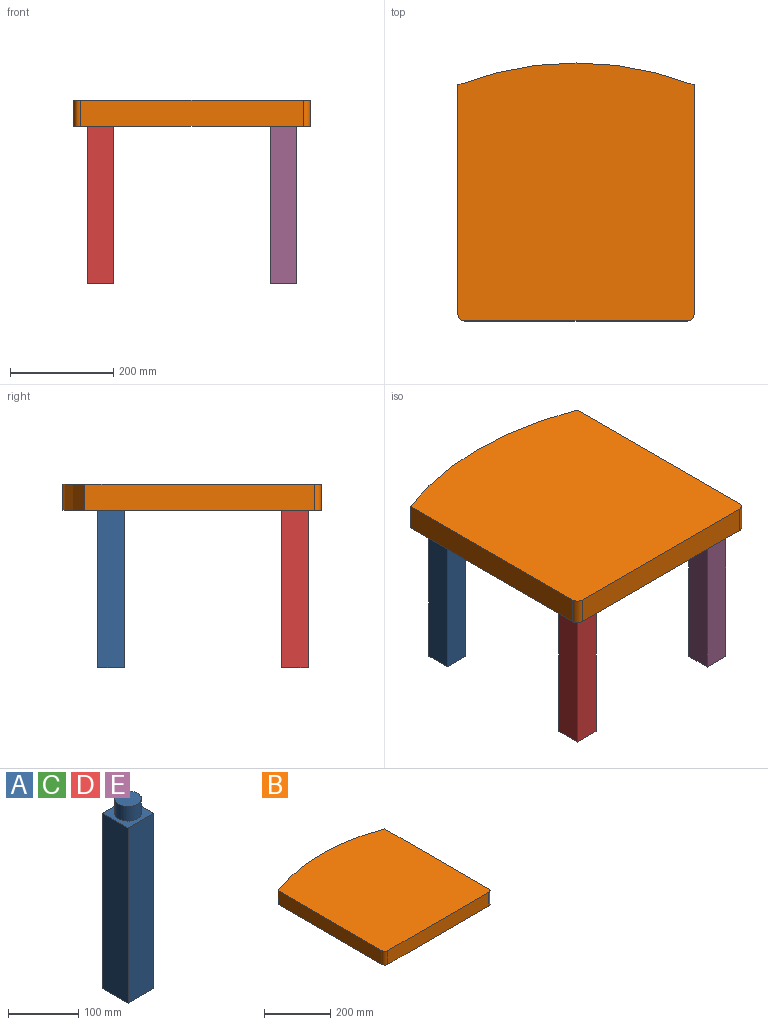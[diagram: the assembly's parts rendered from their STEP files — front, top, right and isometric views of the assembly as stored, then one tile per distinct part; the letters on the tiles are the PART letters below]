
ASSEMBLY  parts=5 mates=4
PART A: 8 faces, bbox 50.8x50.8x330.2 mm
  f0: plane 304.8x50.8mm, normal (0,-1,0), area 15483.8mm2, adj f1,f3,f4,f5
  f1: plane 304.8x50.8mm, normal (-1,0,0), area 15483.8mm2, adj f0,f2,f4,f5
  f2: plane 304.8x50.8mm, normal (0,1,0), area 15483.8mm2, adj f1,f3,f4,f5
  f3: plane 304.8x50.8mm, normal (1,0,0), area 15483.8mm2, adj f0,f2,f4,f5
  f4: plane 50.8x50.8mm, normal (0,0,-1), area 2580.6mm2, adj f0,f1,f2,f3
  f5: plane 50.8x50.8mm, normal (0,0,1), area 1440.5mm2, adj f0,f1,f2,f3,f6
  f6: cylinder r=19.05mm len=38.1mm, axis (0,0,-1), area 3040.2mm2, adj f5,f7
  f7: plane 38.1x38.1mm, normal (0,0,1), area 1140.1mm2, adj f6
PART B: 16 faces, bbox 457.2x499.8x50.8 mm
  f0: plane 499.78x457.2mm, normal (0,0,-1), area 217468.8mm2, adj f1,f2,f3,f4,f5,f6,f8,f10
  f1: plane 444.5x50.8mm, normal (1,0,0), area 22580.6mm2, adj f0,f2,f6,f7
  f2: cylinder r=635mm len=457.2mm, axis (0,0,-1), area 23759.2mm2, adj f0,f1,f3,f7
  f3: plane 444.5x50.8mm, normal (-1,0,0), area 22580.6mm2, adj f0,f2,f4,f7
  f4: cylinder r=12.7mm len=50.8mm, axis (0,0,-1), area 1013.4mm2, adj f0,f3,f5,f7
  f5: plane 431.8x50.8mm, normal (0,-1,0), area 21935.4mm2, adj f0,f4,f6,f7
  f6: cylinder r=12.7mm len=50.8mm, axis (0,0,-1), area 1013.4mm2, adj f0,f1,f5,f7
  f7: plane 499.78x457.2mm, normal (0,0,1), area 222029.1mm2, adj f1,f2,f3,f4,f5,f6
  f8: cylinder r=19.05mm len=38.1mm, axis (0,0,-1), area 3040.2mm2, adj f0,f9
  f9: plane 38.1x38.1mm, normal (0,0,-1), area 1140.1mm2, adj f8
  f10: cylinder r=19.05mm len=38.1mm, axis (0,0,-1), area 3040.2mm2, adj f0,f11
  f11: plane 38.1x38.1mm, normal (0,0,-1), area 1140.1mm2, adj f10
  f12: cylinder r=19.05mm len=38.1mm, axis (0,0,-1), area 3040.2mm2, adj f0,f13
  f13: plane 38.1x38.1mm, normal (0,0,-1), area 1140.1mm2, adj f12
  f14: cylinder r=19.05mm len=38.1mm, axis (0,0,-1), area 3040.2mm2, adj f0,f15
  f15: plane 38.1x38.1mm, normal (0,0,-1), area 1140.1mm2, adj f14
PART C: same geometry as A
PART D: same geometry as A
PART E: same geometry as A
PLACE A t=(-93.55,326.61,-138.94)mm
PLACE B t=(-93.55,-29.62,-138.94)mm
PLACE C t=(262.05,326.61,-138.94)mm
PLACE D t=(-93.55,-29.62,-138.94)mm
PLACE E t=(262.05,-29.62,-138.94)mm
MATE fastened E.f6 <-> B.f14  axis (0,0,1) through (84.25,-207.74,-113.54)mm
MATE fastened D.f6 <-> B.f8  axis (0,0,1) through (-271.35,-207.74,-113.54)mm
MATE fastened A.f6 <-> B.f10  axis (0,0,1) through (-271.35,148.49,-113.54)mm
MATE fastened C.f6 <-> B.f12  axis (0,0,1) through (84.25,148.49,-113.54)mm
